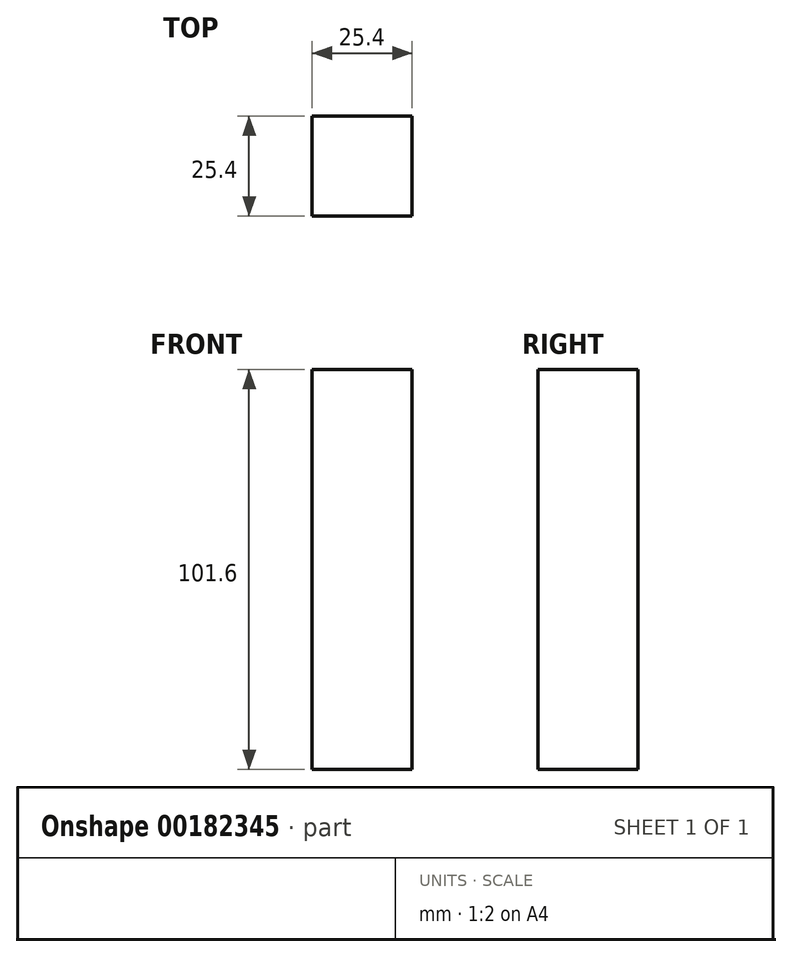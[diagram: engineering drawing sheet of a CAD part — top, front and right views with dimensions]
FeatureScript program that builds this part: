
annotation { "Feature Type Name" : "Feature", "Feature Type Description" : "" }
export const myFeature = defineFeature(function(context is Context, id is Id, definition is map)
    precondition{}
    {
        {
            var Q0;
            Q0=qCreatedBy(makeId("Front.planeOp"),FACE);
            var sketch = newSketch(context, id + "F0", { "sketchPlane" : qUnion([Q0])});
            skLineSegment(sketch, "E0", {"start": v(-25.4, 54.64) * mm, "end": v(-25.4, -46.96) * mm});
            skLineSegment(sketch, "E1", {"start": v(-25.4, 54.64) * mm, "end": v(0, 54.64) * mm});
            skLineSegment(sketch, "E2", {"start": v(0, 54.64) * mm, "end": v(0, -46.96) * mm});
            skLineSegment(sketch, "E3", {"start": v(0, -46.96) * mm, "end": v(-25.4, -46.96) * mm});
            skSolve(sketch);
        }
        {
            var Q0;
            Q0=makeQuery(id+"F0.imprint","IMPRINT",FACE,{"disambiguationData":[TD([[makeQuery(id+"F0.imprint","IMPRINT",EDGE,{"derivedFrom":sQuery(id+"F0.wireOp",EDGE,"E0")}),1.0]])]});
            var Q1;
            Q1 = qSketchRegion(id + "FBfrtfTa3IHkZqv_1", true);
            extrude(context, id + "F1", {"entities" : qUnion([Q0, Q1]), "depth" : 25.4 * mm});
        }
    });
